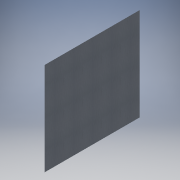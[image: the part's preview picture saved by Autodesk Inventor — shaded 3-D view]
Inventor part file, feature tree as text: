
AUTODESK INVENTOR PART (.ipt)
format: ipt  version: 2018 (Build 220112000, 112)  size: 100,864 bytes
history: native  units: mm
features: other x3, sketch x1
ambient origin geometry x8: Origin, YZ Plane, XZ Plane, XY Plane, X Axis, Y Axis, Z Axis, Center Point
bodies: Volumenkörper1 (feature_tree)
feature tree (4):
  other  "Wand2.ipt"
  other  "Volumenkörper1::Wand2.ipt"
  other  "Bezeichnung1"
  sketch  "Skizze1"  dims[d0=10.0mm]
